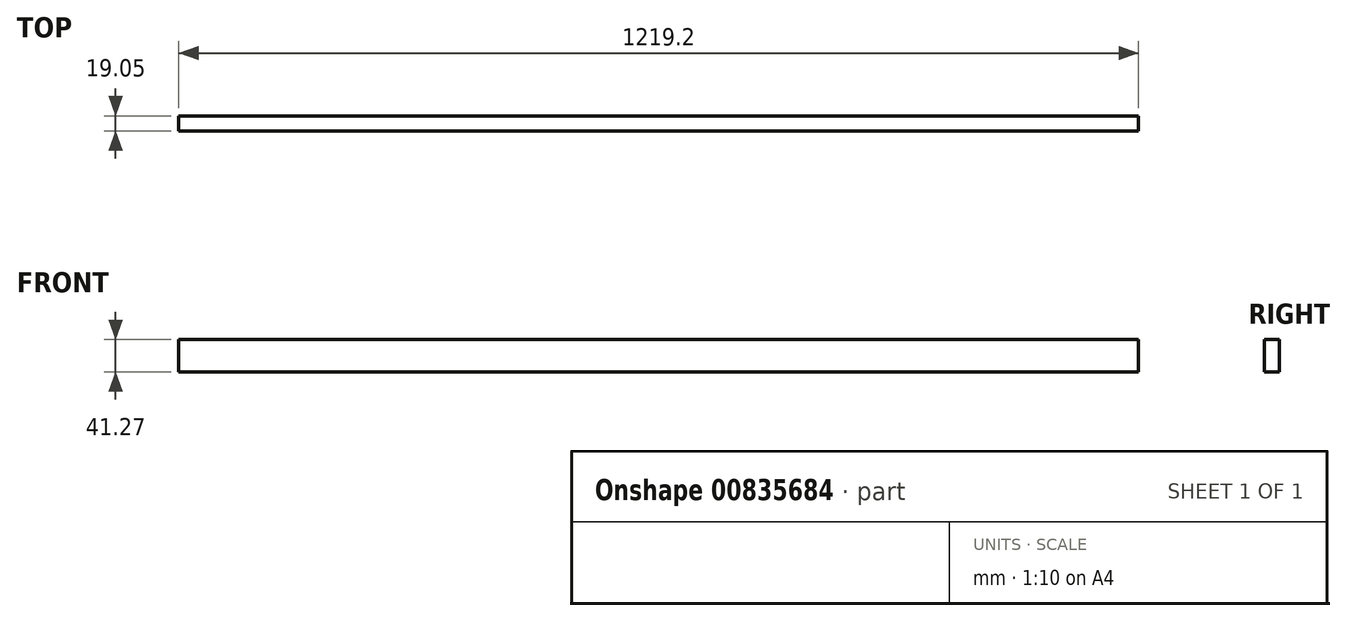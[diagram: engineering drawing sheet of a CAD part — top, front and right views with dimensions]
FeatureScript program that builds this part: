
annotation { "Feature Type Name" : "Feature", "Feature Type Description" : "" }
export const myFeature = defineFeature(function(context is Context, id is Id, definition is map)
    precondition{}
    {
        {
            var Q0;
            Q0=qCreatedBy(makeId("Front.planeOp"),FACE);
            var sketch = newSketch(context, id + "F0", { "sketchPlane" : qUnion([Q0])});
            skLineSegment(sketch, "E0.bottom", {"start": v(0, 0) * mm, "end": v(1219.2, 0) * mm});
            skLineSegment(sketch, "E0.top", {"start": v(0, 41.28) * mm, "end": v(1219.2, 41.28) * mm});
            skLineSegment(sketch, "E0.left", {"start": v(0, 0) * mm, "end": v(0, 41.28) * mm});
            skLineSegment(sketch, "E0.right", {"start": v(1219.2, 0) * mm, "end": v(1219.2, 41.28) * mm});
            skSolve(sketch);
        }
        {
            var Q0;
            Q0 = qSketchRegion(id + "F0", true);
            extrude(context, id + "F1", {"entities" : qUnion([Q0]), "depth" : 19.05 * mm, "offsetDistance" : 25.4 * mm});
        }
    });
